# Revit family: Dynamic Fenestration - Outswing Casement - Bevel SDL
name_source: partatom
category: Windows
units: mm (PartAtom-declared; Revit-internal decimal feet)

## family parameters
Always vertical = Yes
Cut with Voids When Loaded = No
Host = Wall
OmniClass Number = 23.30.20.00
OmniClass Title = Windows
Room Calculation Point = No
Shared = No

## types (1)
- 60" x 36"
    Analytic Construction = <None>
    Default Sill Height = 36"
    Define Thermal Properties by = Schematic Type
    Description = Outswing Casement - Bevel SDL
    Frame Material = Arte Metal
    Gap Fill = Argon
    Glass Material = Glass
    Glass Type = Triple Silve LowE / Clear
    Handle Height = 30"
    Height = 54 1/2"
    Manufacturer = Dynamic Fenestration
    Max. Height = 84"
    Max. Width = 48"
    Min. Height = 16"
    Min. Width = 12"
    Model = Outswing Casement
    Rough Height = 60"
    Rough Width = 36"
    Rubber Material = Rubber
    Wall Closure = By host
    Width = 30 1/2"

## geometry (parser evidence)
native form markers: Sweep x21
no freeform markers — native parametric forms only
